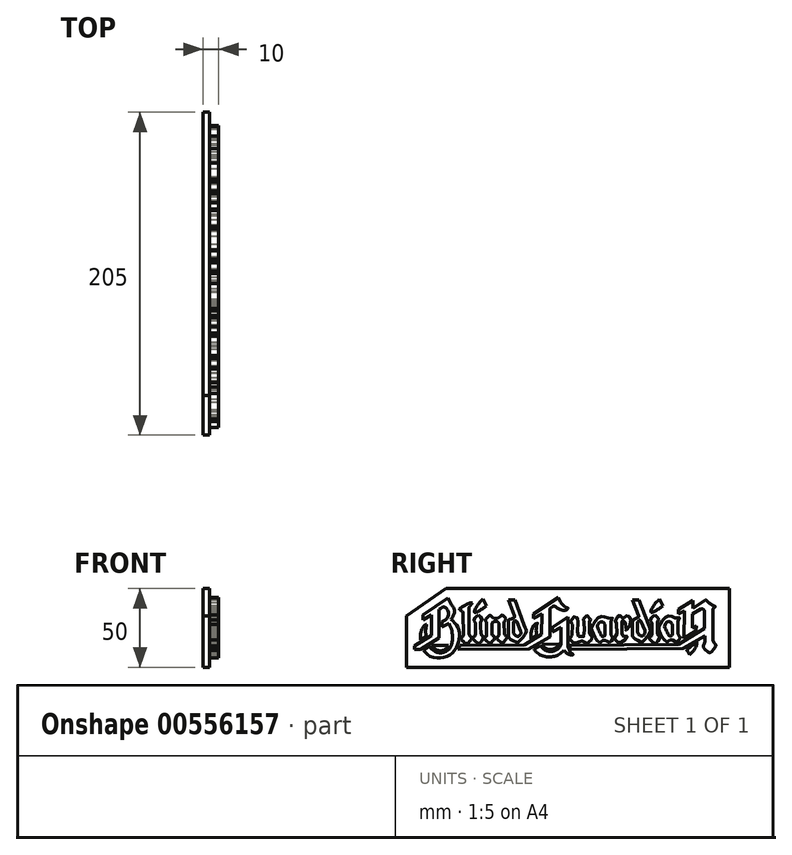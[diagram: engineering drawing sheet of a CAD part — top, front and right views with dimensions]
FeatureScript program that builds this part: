
annotation { "Feature Type Name" : "Feature", "Feature Type Description" : "" }
export const myFeature = defineFeature(function(context is Context, id is Id, definition is map)
    precondition{}
    {
        {
            var Q0;
            Q0=qCreatedBy(makeId("Right.planeOp"),FACE);
            var sketch = newSketch(context, id + "F0", { "sketchPlane" : qUnion([Q0])});
            skLineSegment(sketch, "E0", {"start": v(-84.73, 5.08) * mm, "end": v(-84.73, 8.23) * mm});
            skLineSegment(sketch, "E1", {"start": v(-84.73, 8.23) * mm, "end": v(-68.64, 19.15) * mm});
            skLineSegment(sketch, "E2", {"start": v(-84.73, 5.08) * mm, "end": v(-79.13, 8.3) * mm});
            skLineSegment(sketch, "E3", {"start": v(-79.13, 8.3) * mm, "end": v(-79.13, -4.84) * mm});
            skLineSegment(sketch, "E4", {"start": v(-79.13, -4.84) * mm, "end": v(-90.14, -11.45) * mm});
            skLineSegment(sketch, "E5", {"start": v(-90.14, -11.45) * mm, "end": v(-90.14, -13.8) * mm});
            skLineSegment(sketch, "E6", {"start": v(-90.14, -13.8) * mm, "end": v(-86.17, -13.8) * mm});
            skLineSegment(sketch, "E7", {"start": v(-86.17, -13.8) * mm, "end": v(-74.29, -6.5) * mm});
            skLineSegment(sketch, "E8", {"start": v(-74.29, -6.5) * mm, "end": v(-74.29, 11.65) * mm});
            skFitSpline(sketch, "E9", {"points": [v(-68.64, 19.15) * mm, v(-67.18, 15.64) * mm, v(-65.24, 13) * mm, v(-64.6, 11.06) * mm, v(-65.24, 7.93) * mm, v(-66.75, 5.45) * mm], "startDerivative": vector(5.4, -16.3) * mm, "endDerivative": vector(-8.46, -11.7) * mm});
            skFitSpline(sketch, "E10", {"points": [v(-66.75, 5.45) * mm, v(-64.43, 3.18) * mm, v(-62, -0.73) * mm, v(-61.43, -4.8) * mm, v(-62.17, -9.59) * mm, v(-64.56, -14.4) * mm, v(-69.3, -18.01) * mm, v(-75.07, -19.05) * mm, v(-81.23, -17.36) * mm, v(-84.19, -14.28) * mm], "startDerivative": vector(25.48, -22.56) * mm, "endDerivative": vector(-23.63, 32.62) * mm});
            skLineSegment(sketch, "E11", {"start": v(-84.19, -14.28) * mm, "end": v(-80.47, -11.9) * mm});
            skFitSpline(sketch, "E12", {"points": [v(-80.47, -11.9) * mm, v(-78.16, -14.27) * mm, v(-74.24, -15.81) * mm, v(-69.63, -14.76) * mm, v(-66.48, -10.92) * mm, v(-65.96, -4.87) * mm, v(-66.52, -0.7) * mm, v(-68.23, 3) * mm], "startDerivative": vector(16.74, -20.43) * mm, "endDerivative": vector(-14.61, 26.93) * mm});
            skFitSpline(sketch, "E13", {"points": [v(-74.29, 11.65) * mm, v(-72.46, 13.03) * mm, v(-70.92, 13.2) * mm, v(-68.82, 11.08) * mm, v(-68.76, 7.13) * mm, v(-70.78, 4.75) * mm, v(-72.57, 3.77) * mm], "startDerivative": vector(11.7, 10.28) * mm, "endDerivative": vector(-11.83, -5.55) * mm});
            skLineSegment(sketch, "E14", {"start": v(-68.23, 3) * mm, "end": v(-72.57, 0.76) * mm});
            skLineSegment(sketch, "E15", {"start": v(-72.57, 0.76) * mm, "end": v(-72.57, 3.77) * mm});
            skLineSegment(sketch, "E16", {"start": v(-79.14, -11.26) * mm, "end": v(-68.4, -10.98) * mm});
            skFitSpline(sketch, "E17", {"points": [v(-68.4, -10.98) * mm, v(-69.8, -13.08) * mm, v(-72.6, -14.4) * mm, v(-75.7, -14.13) * mm, v(-77.95, -12.73) * mm, v(-79.14, -11.26) * mm], "startDerivative": vector(-5.81, -11.49) * mm, "endDerivative": vector(-6.19, 8.83) * mm});
            skLineSegment(sketch, "E18", {"start": v(-82.4, -5.4) * mm, "end": v(-86.28, -7.61) * mm});
            skFitSpline(sketch, "E19", {"points": [v(-82.4, -5.4) * mm, v(-82.8, -3.93) * mm, v(-82.85, -1.08) * mm, v(-82.23, 2.17) * mm], "startDerivative": vector(-1.73, 5.13) * mm, "endDerivative": vector(2, 8.42) * mm});
            skFitSpline(sketch, "E20", {"points": [v(-86.28, -7.61) * mm, v(-86.28, -5.4) * mm, v(-85.85, -2.26) * mm, v(-84.59, 0.4) * mm, v(-83.33, 1.73) * mm, v(-82.23, 2.17) * mm], "startDerivative": vector(-0.23, 10.54) * mm, "endDerivative": vector(7.6, 2.22) * mm});
            skFitSpline(sketch, "E21", {"points": [v(-59.1, 9.06) * mm, v(-59.28, 10.1) * mm, v(-60.1, 10.84) * mm, v(-61.1, 11.4) * mm, v(-61.5, 11.83) * mm, v(-60.67, 12.62) * mm, v(-58.24, 14.18) * mm, v(-54.85, 15.7) * mm, v(-53.12, 16) * mm], "startDerivative": vector(-0.2, 10.77) * mm, "endDerivative": vector(11.85, 1.15) * mm});
            skFitSpline(sketch, "E22", {"points": [v(-53.12, 16) * mm, v(-53.9, 14.96) * mm, v(-54.94, 13.57) * mm, v(-55.42, 12.62) * mm, v(-55.46, 11.92) * mm], "startDerivative": vector(-2.78, -3.76) * mm, "endDerivative": vector(0.11, -3.55) * mm});
            skLineSegment(sketch, "E23", {"start": v(-55.46, 11.92) * mm, "end": v(-55.46, -3.28) * mm});
            skLineSegment(sketch, "E24", {"start": v(-59.1, 9.06) * mm, "end": v(-58.91, -4.41) * mm});
            skFitSpline(sketch, "E25", {"points": [v(-58.91, -4.41) * mm, v(-59.17, -5.41) * mm, v(-60.16, -6.23) * mm, v(-60.62, -6.6) * mm, v(-60.41, -7.13) * mm, v(-59.8, -7.86) * mm, v(-58.91, -8.77) * mm, v(-57.4, -10) * mm, v(-56.99, -10.22) * mm, v(-56.42, -9.92) * mm, v(-54.9, -8.63) * mm, v(-53.72, -6.82) * mm, v(-53.59, -6.32) * mm, v(-53.82, -5.96) * mm, v(-54.52, -5.39) * mm, v(-55.08, -4.66) * mm, v(-55.36, -3.82) * mm, v(-55.46, -3.28) * mm], "startDerivative": vector(-1.38, -16.95) * mm, "endDerivative": vector(-1.94, 11.37) * mm});
            skFitSpline(sketch, "E26", {"points": [v(-46.43, 18.3) * mm, v(-47.6, 17.21) * mm, v(-49.28, 15.37) * mm, v(-50.45, 13.61) * mm, v(-51.62, 11.52) * mm, v(-51.95, 10.52) * mm, v(-51.95, 9.89) * mm, v(-51.12, 9.85) * mm, v(-49.6, 10.4) * mm, v(-48.27, 11.19) * mm, v(-46.76, 12.27) * mm, v(-45.43, 13.24) * mm, v(-44.38, 13.95) * mm], "startDerivative": vector(-13.02, -11.66) * mm, "endDerivative": vector(13.48, 9.05) * mm});
            skLineSegment(sketch, "E27", {"start": v(-44.38, 13.95) * mm, "end": v(-46.43, 18.3) * mm});
            skFitSpline(sketch, "E28", {"points": [v(-49.36, 8.34) * mm, v(-50.32, 7.67) * mm, v(-51.53, 6.42) * mm, v(-52.46, 5.08) * mm, v(-51.53, 3.74) * mm, v(-51.37, 2.73) * mm, v(-51.28, -3.96) * mm, v(-51.45, -4.63) * mm, v(-52.04, -5.47) * mm, v(-53.2, -6.22) * mm, v(-52.88, -6.96) * mm, v(-51.47, -8.5) * mm, v(-50.33, -9.43) * mm, v(-49.4, -10.02) * mm, v(-48.65, -9.53) * mm, v(-47.13, -8.04) * mm, v(-46.26, -6.5) * mm, v(-46.1, -5.95) * mm, v(-47.08, -5.03) * mm, v(-47.67, -4.38) * mm, v(-47.84, -3.24) * mm, v(-47.94, 3.03) * mm, v(-47.78, 3.92) * mm, v(-47.21, 4.84) * mm, v(-46.97, 5.17) * mm, v(-47.02, 5.55) * mm, v(-48.13, 6.93) * mm, v(-49.36, 8.34) * mm]});
            skLineSegment(sketch, "E29", {"start": v(-44.12, 3.65) * mm, "end": v(-44.12, -4.8) * mm});
            skLineSegment(sketch, "E30", {"start": v(-40.75, 2.67) * mm, "end": v(-40.75, -3.66) * mm});
            skLineSegment(sketch, "E31", {"start": v(-36.33, 2.6) * mm, "end": v(-36.33, -4.34) * mm});
            skLineSegment(sketch, "E32", {"start": v(-33.03, 3.34) * mm, "end": v(-32.9, -3.77) * mm});
            skFitSpline(sketch, "E33", {"points": [v(-33.03, 3.34) * mm, v(-32.77, 4.26) * mm, v(-32.17, 5.1) * mm, v(-32, 5.39) * mm, v(-32.07, 5.74) * mm, v(-33.17, 7.2) * mm, v(-34.04, 8.1) * mm, v(-34.3, 8.27) * mm, v(-34.65, 8.12) * mm, v(-35.37, 7.4) * mm, v(-36.57, 6.48) * mm, v(-37.62, 6.02) * mm, v(-38.75, 5.99) * mm, v(-40.12, 6.44) * mm, v(-41.35, 7.36) * mm, v(-41.86, 7.92) * mm, v(-42, 8.06) * mm, v(-42.15, 8.12) * mm, v(-42.4, 8) * mm, v(-43.13, 7.34) * mm, v(-43.9, 6.48) * mm, v(-44.6, 5.6) * mm, v(-44.9, 5.21) * mm, v(-44.96, 5.04) * mm, v(-44.82, 4.72) * mm, v(-44.52, 4.25) * mm, v(-44.33, 3.98) * mm, v(-44.12, 3.65) * mm], "startDerivative": vector(3.75, 21.25) * mm, "endDerivative": vector(7.67, -12.75) * mm});
            skFitSpline(sketch, "E34", {"points": [v(-40.75, 2.67) * mm, v(-40.28, 3.54) * mm, v(-39.14, 4.03) * mm, v(-37.8, 4.07) * mm, v(-36.76, 3.49) * mm, v(-36.33, 2.6) * mm], "startDerivative": vector(1.78, 5.2) * mm, "endDerivative": vector(1.63, -5.1) * mm});
            skFitSpline(sketch, "E35", {"points": [v(-32.9, -3.77) * mm, v(-32.57, -4.4) * mm, v(-32, -5.08) * mm, v(-31.39, -5.6) * mm, v(-31.16, -5.82) * mm, v(-31.27, -6.2) * mm, v(-31.88, -7.3) * mm, v(-33.27, -8.8) * mm, v(-34.08, -9.4) * mm, v(-34.47, -9.62) * mm, v(-34.78, -9.44) * mm, v(-35.63, -8.77) * mm, v(-36.93, -7.64) * mm, v(-37.81, -6.55) * mm, v(-37.95, -6.27) * mm, v(-37.72, -5.97) * mm, v(-36.93, -5.43) * mm, v(-36.33, -4.87) * mm, v(-36.33, -4.55) * mm, v(-36.33, -4.34) * mm], "startDerivative": vector(5.52, -12.4) * mm, "endDerivative": vector(0.48, 7.16) * mm});
            skFitSpline(sketch, "E36", {"points": [v(-40.75, -3.66) * mm, v(-40.59, -4.34) * mm, v(-39.9, -5.08) * mm, v(-39.1, -5.69) * mm, v(-38.84, -5.89) * mm, v(-38.93, -6.28) * mm, v(-39.52, -7.37) * mm, v(-41.46, -9.3) * mm, v(-42.08, -9.73) * mm, v(-42.34, -9.73) * mm, v(-42.84, -9.47) * mm, v(-45.13, -7.41) * mm, v(-45.61, -6.72) * mm, v(-45.64, -6.39) * mm, v(-45.27, -6.02) * mm, v(-44.5, -5.4) * mm, v(-44.12, -5.08) * mm, v(-44.12, -4.8) * mm], "startDerivative": vector(1.18, -12.53) * mm, "endDerivative": vector(-1.63, 8.17) * mm});
            skFitSpline(sketch, "E37", {"points": [v(-26.5, 7.68) * mm, v(-26.37, 7.09) * mm, v(-26.48, 6.65) * mm, v(-27.5, 6.19) * mm, v(-28.84, 5.6) * mm, v(-29.9, 5) * mm, v(-30.38, 4.34) * mm, v(-30.44, 3.34) * mm, v(-30.43, -5.08) * mm, v(-30.4, -5.49) * mm, v(-29.76, -6.52) * mm, v(-27.07, -8.3) * mm, v(-25.06, -9.14) * mm, v(-24.72, -9.24) * mm, v(-24.38, -9.18) * mm, v(-23.02, -7.9) * mm, v(-20.64, -5.23) * mm, v(-19.05, -2.95) * mm, v(-18.92, -2.3) * mm, v(-19.1, -1.2) * mm, v(-19.5, -0.04) * mm, v(-20.36, 1.92) * mm], "startDerivative": vector(5.75, -19.57) * mm, "endDerivative": vector(-15.94, 36.18) * mm});
            skLineSegment(sketch, "E38", {"start": v(-26.5, 7.68) * mm, "end": v(-30.31, 17.65) * mm});
            skLineSegment(sketch, "E39", {"start": v(-30.31, 17.65) * mm, "end": v(-26.19, 17.65) * mm});
            skLineSegment(sketch, "E40", {"start": v(-26.19, 17.65) * mm, "end": v(-20.36, 1.92) * mm});
            skLineSegment(sketch, "E41", {"start": v(-27.18, -2.48) * mm, "end": v(-27.18, 3.19) * mm});
            skLineSegment(sketch, "E42", {"start": v(-25, 3.9) * mm, "end": v(-22.62, -1.86) * mm});
            skFitSpline(sketch, "E43", {"points": [v(-27.18, 3.19) * mm, v(-26.96, 3.92) * mm, v(-26.3, 4.44) * mm, v(-25.44, 4.46) * mm, v(-25, 3.9) * mm], "startDerivative": vector(0.53, 3.15) * mm, "endDerivative": vector(1.42, -2.93) * mm});
            skFitSpline(sketch, "E44", {"points": [v(-22.62, -1.86) * mm, v(-22.43, -2.56) * mm, v(-22.43, -3.43) * mm, v(-23.62, -5.17) * mm, v(-24, -5.39) * mm, v(-24.6, -5.39) * mm, v(-25.58, -4.98) * mm, v(-26.44, -4.36) * mm, v(-27.1, -3.27) * mm, v(-27.18, -2.48) * mm], "startDerivative": vector(1.99, -7.25) * mm, "endDerivative": vector(0.09, 7.38) * mm});
            skFitSpline(sketch, "E45", {"points": [v(-12.08, -4.65) * mm, v(-12.67, -2.48) * mm, v(-12.58, -0.04) * mm, v(-11.91, 3.05) * mm, v(-11.86, 3.14) * mm, v(-12.2, 3.02) * mm, v(-13.75, 1.95) * mm, v(-15.06, -0.04) * mm, v(-15.73, -2.07) * mm, v(-15.95, -4.23) * mm, v(-16, -6.42) * mm, v(-16.01, -6.71) * mm, v(-16.01, -6.8) * mm, v(-13.95, -5.58) * mm, v(-12.27, -4.7) * mm], "startDerivative": vector(-8.11, 24.7) * mm, "endDerivative": vector(17.5, 8) * mm});
            skLineSegment(sketch, "E46", {"start": v(-12.27, -4.7) * mm, "end": v(-12.08, -4.65) * mm});
            skLineSegment(sketch, "E47", {"start": v(-8.92, -10.51) * mm, "end": v(1.73, -10.24) * mm});
            skArc(sketch, "E48", {"start": v(-8.92, -10.51) * mm, "mid": v(-3.5, -13.74) * mm, "end": v(1.73, -10.24) * mm});
            skLineSegment(sketch, "E49", {"start": v(-62.44, -13.6) * mm, "end": v(-61.23, -11.18) * mm});
            skLineSegment(sketch, "E50", {"start": v(-61.23, -11.18) * mm, "end": v(-20.11, -10.87) * mm});
            skLineSegment(sketch, "E51", {"start": v(-20.11, -10.87) * mm, "end": v(-9.26, -4.14) * mm});
            skLineSegment(sketch, "E52", {"start": v(-9.26, -4.14) * mm, "end": v(-8.92, 8.96) * mm});
            skLineSegment(sketch, "E53", {"start": v(-8.92, 8.96) * mm, "end": v(-14.41, 6) * mm});
            skLineSegment(sketch, "E54", {"start": v(-14.41, 6) * mm, "end": v(-14.49, 8.88) * mm});
            skLineSegment(sketch, "E55", {"start": v(-14.49, 8.88) * mm, "end": v(1.35, 19.49) * mm});
            skLineSegment(sketch, "E56", {"start": v(-3.84, 12.28) * mm, "end": v(-3.84, -5.2) * mm});
            skLineSegment(sketch, "E57", {"start": v(-62.44, -13.6) * mm, "end": v(-17.17, -13.28) * mm});
            skLineSegment(sketch, "E58", {"start": v(-17.17, -13.28) * mm, "end": v(-4.43, -6.18) * mm});
            skFitSpline(sketch, "E59", {"points": [v(-4.43, -6.18) * mm, v(-4, -5.78) * mm, v(-3.84, -5.2) * mm], "startDerivative": vector(1, 0.73) * mm, "endDerivative": vector(0.2, 1.22) * mm});
            skFitSpline(sketch, "E60", {"points": [v(-3.84, 12.28) * mm, v(-2.14, 13.6) * mm, v(-1.54, 13.8) * mm, v(-0.94, 13.78) * mm, v(-0.17, 13.29) * mm, v(0.9, 12.48) * mm, v(2.68, 11.54) * mm, v(4.55, 11.25) * mm, v(6.3, 11.46) * mm, v(7.47, 12.28) * mm, v(7.62, 12.5) * mm, v(7.64, 12.55) * mm, v(6.1, 13.15) * mm, v(4.2, 14.6) * mm, v(2.78, 16.44) * mm, v(1.55, 18.96) * mm, v(1.35, 19.49) * mm], "startDerivative": vector(23.38, 19.98) * mm, "endDerivative": vector(-3.54, 9.98) * mm});
            skFitSpline(sketch, "E61", {"points": [v(52.4, 7.87) * mm, v(52.54, 7.28) * mm, v(52.43, 6.85) * mm, v(51.4, 6.38) * mm, v(50.07, 5.79) * mm, v(49, 5.2) * mm, v(48.52, 4.54) * mm, v(48.47, 3.54) * mm, v(48.47, -4.88) * mm, v(48.5, -5.3) * mm, v(49.14, -6.32) * mm, v(51.83, -8.1) * mm, v(53.85, -8.95) * mm, v(54.19, -9.04) * mm, v(54.53, -8.99) * mm, v(55.89, -7.71) * mm, v(58.27, -5.04) * mm, v(59.85, -2.76) * mm, v(59.98, -2.1) * mm, v(59.81, -1.01) * mm, v(59.4, 0.16) * mm, v(58.55, 2.12) * mm], "startDerivative": vector(5.75, -19.57) * mm, "endDerivative": vector(-15.94, 36.18) * mm});
            skLineSegment(sketch, "E62", {"start": v(52.4, 7.87) * mm, "end": v(48.6, 17.85) * mm});
            skLineSegment(sketch, "E63", {"start": v(48.6, 17.85) * mm, "end": v(52.72, 17.85) * mm});
            skLineSegment(sketch, "E64", {"start": v(52.72, 17.85) * mm, "end": v(58.55, 2.12) * mm});
            skLineSegment(sketch, "E65", {"start": v(51.73, -2.29) * mm, "end": v(51.73, 3.38) * mm});
            skLineSegment(sketch, "E66", {"start": v(53.9, 4.09) * mm, "end": v(56.29, -1.67) * mm});
            skFitSpline(sketch, "E67", {"points": [v(51.73, 3.38) * mm, v(51.95, 4.11) * mm, v(52.6, 4.63) * mm, v(53.46, 4.66) * mm, v(53.9, 4.09) * mm], "startDerivative": vector(0.53, 3.15) * mm, "endDerivative": vector(1.42, -2.93) * mm});
            skFitSpline(sketch, "E68", {"points": [v(56.29, -1.67) * mm, v(56.48, -2.37) * mm, v(56.48, -3.24) * mm, v(55.28, -4.98) * mm, v(54.9, -5.2) * mm, v(54.3, -5.2) * mm, v(53.33, -4.79) * mm, v(52.46, -4.16) * mm, v(51.8, -3.08) * mm, v(51.73, -2.29) * mm], "startDerivative": vector(1.99, -7.25) * mm, "endDerivative": vector(0.09, 7.38) * mm});
            skFitSpline(sketch, "E69", {"points": [v(65.7, 18.33) * mm, v(64.53, 17.24) * mm, v(62.86, 15.4) * mm, v(61.69, 13.65) * mm, v(60.52, 11.55) * mm, v(60.18, 10.55) * mm, v(60.18, 9.92) * mm, v(61.02, 9.88) * mm, v(62.53, 10.42) * mm, v(63.86, 11.22) * mm, v(65.37, 12.3) * mm, v(66.7, 13.27) * mm, v(67.76, 13.98) * mm], "startDerivative": vector(-13.02, -11.66) * mm, "endDerivative": vector(13.48, 9.05) * mm});
            skLineSegment(sketch, "E70", {"start": v(67.76, 13.98) * mm, "end": v(65.7, 18.33) * mm});
            skFitSpline(sketch, "E71", {"points": [v(62.78, 8.37) * mm, v(61.81, 7.7) * mm, v(60.6, 6.45) * mm, v(59.68, 5.1) * mm, v(60.6, 3.77) * mm, v(60.77, 2.77) * mm, v(60.85, -3.93) * mm, v(60.68, -4.6) * mm, v(60.1, -5.43) * mm, v(58.93, -6.19) * mm, v(59.25, -6.92) * mm, v(60.66, -8.47) * mm, v(61.8, -9.4) * mm, v(62.73, -9.99) * mm, v(63.49, -9.5) * mm, v(65, -8) * mm, v(65.87, -6.46) * mm, v(66.04, -5.92) * mm, v(65.06, -5) * mm, v(64.46, -4.35) * mm, v(64.3, -3.2) * mm, v(64.2, 3.06) * mm, v(64.35, 3.96) * mm, v(64.92, 4.88) * mm, v(65.17, 5.2) * mm, v(65.11, 5.58) * mm, v(64, 6.97) * mm, v(62.78, 8.37) * mm]});
            skLineSegment(sketch, "E72", {"start": v(2.94, -10.45) * mm, "end": v(3.12, 0.38) * mm});
            skLineSegment(sketch, "E73", {"start": v(3.12, 0.38) * mm, "end": v(-2.25, -2.44) * mm});
            skLineSegment(sketch, "E74", {"start": v(-2.25, -2.44) * mm, "end": v(-2.25, 0.38) * mm});
            skLineSegment(sketch, "E75", {"start": v(-2.25, 0.38) * mm, "end": v(7.42, 6.85) * mm});
            skLineSegment(sketch, "E76", {"start": v(7.42, 6.85) * mm, "end": v(7.42, -10.2) * mm});
            skFitSpline(sketch, "E77", {"points": [v(7.42, -10.2) * mm, v(7.63, -12.34) * mm, v(9.05, -15.25) * mm, v(10.63, -17.04) * mm, v(10.72, -17.11) * mm, v(10.6, -17.11) * mm, v(9.17, -17.04) * mm, v(6.72, -16.08) * mm, v(5.06, -14.44) * mm], "startDerivative": vector(0.17, -13.92) * mm, "endDerivative": vector(-9.57, 11.37) * mm});
            skLineSegment(sketch, "E78", {"start": v(-14.13, -13.4) * mm, "end": v(-10.36, -11.11) * mm});
            skFitSpline(sketch, "E79", {"points": [v(-14.13, -13.4) * mm, v(-12.99, -15.09) * mm, v(-10.5, -16.89) * mm, v(-7.4, -18.12) * mm, v(-4, -18.42) * mm, v(-0.9, -17.92) * mm, v(2.07, -16.64) * mm, v(4.47, -14.82) * mm, v(5.06, -14.44) * mm], "startDerivative": vector(8.5, -15.86) * mm, "endDerivative": vector(7.8, 4.28) * mm});
            skFitSpline(sketch, "E80", {"points": [v(-10.36, -11.11) * mm, v(-8.28, -13.14) * mm, v(-5.18, -14.72) * mm, v(-1.61, -14.68) * mm, v(1.51, -12.97) * mm, v(2.94, -10.45) * mm], "startDerivative": vector(10.06, -11.04) * mm, "endDerivative": vector(6.18, 13.54) * mm});
            skFitSpline(sketch, "E81", {"points": [v(10.19, -4.82) * mm, v(10.25, 1.64) * mm, v(10.25, 2.47) * mm, v(10.16, 2.86) * mm, v(9.72, 3.7) * mm, v(9.29, 4.17) * mm, v(9.11, 4.46) * mm, v(9.37, 4.83) * mm, v(10.8, 6.72) * mm, v(11.81, 7.6) * mm, v(12.15, 7.76) * mm, v(12.55, 7.5) * mm, v(14.24, 5.47) * mm, v(14.57, 4.96) * mm, v(14.1, 4.12) * mm, v(13.7, 3.14) * mm, v(13.56, -0.76) * mm, v(13.63, -4) * mm, v(13.67, -4.54) * mm, v(14.07, -5.21) * mm, v(15.28, -5.99) * mm, v(16.4, -6.02) * mm, v(17.47, -5.48) * mm, v(17.94, -4.74) * mm, v(17.98, -3.16) * mm, v(17.94, 2.13) * mm, v(17.94, 2.8) * mm, v(17.6, 3.62) * mm, v(16.87, 4.5) * mm, v(16.78, 4.76) * mm, v(17.25, 5.48) * mm, v(18.18, 6.59) * mm, v(19.32, 7.65) * mm, v(19.6, 7.82) * mm, v(19.9, 7.78) * mm, v(20.79, 6.86) * mm, v(21.58, 5.85) * mm, v(21.98, 5.28) * mm, v(22.1, 5.09) * mm, v(22, 4.83) * mm, v(21.43, 4.04) * mm, v(21.3, 3.84) * mm, v(21.24, 3.46) * mm, v(21.28, -3.67) * mm, v(21.28, -3.92) * mm, v(21.63, -4.78) * mm, v(22.58, -5.52) * mm, v(23.15, -5.63) * mm, v(23.26, -5.63) * mm, v(23.28, -5.82) * mm, v(22.97, -6.84) * mm, v(21.6, -8.54) * mm, v(20.08, -9.75) * mm, v(19.84, -9.83) * mm, v(19.5, -9.66) * mm, v(18.45, -8.95) * mm, v(16.83, -8.25) * mm, v(15.87, -8.08) * mm, v(14.57, -8.27) * mm, v(12.33, -9.73) * mm, v(11.97, -10.13) * mm, v(11.77, -10.2) * mm, v(11.12, -9.78) * mm, v(9.8, -8.64) * mm, v(8.74, -7.43) * mm, v(8.52, -7.13) * mm, v(8.57, -6.77) * mm, v(9.42, -6.22) * mm, v(10.12, -5.53) * mm, v(10.19, -4.82) * mm]});
            skFitSpline(sketch, "E82", {"points": [v(36.88, -6.22) * mm, v(38.1, -5.21) * mm, v(38.45, -4.03) * mm, v(38.4, 2.82) * mm, v(38.38, 3.27) * mm, v(38.27, 3.67) * mm, v(37.56, 4.55) * mm, v(37.39, 4.75) * mm, v(37.4, 5.05) * mm, v(39.2, 7.26) * mm, v(39.98, 7.94) * mm, v(40.22, 8.05) * mm, v(40.57, 7.9) * mm, v(41.8, 6.65) * mm, v(42.32, 6.06) * mm, v(42.5, 5.97) * mm, v(42.67, 6.1) * mm, v(44.02, 7.28) * mm, v(44.96, 7.96) * mm, v(45.29, 8.07) * mm, v(45.64, 7.8) * mm, v(46.51, 6.85) * mm, v(47.3, 5.75) * mm, v(47.56, 4.46) * mm, v(47.21, 2.72) * mm, v(46.51, 1.08) * mm, v(45.55, -0.32) * mm, v(44.41, -1.41) * mm, v(44.27, -1.54) * mm, v(44.27, -1.41) * mm, v(44.32, 0.79) * mm, v(44.23, 2.3) * mm, v(43.38, 4.04) * mm, v(42.81, 4.72) * mm, v(42.55, 4.8) * mm, v(42.16, 4.55) * mm, v(41.8, 3.98) * mm, v(41.72, 2.71) * mm, v(41.73, -3.84) * mm, v(41.77, -4.09) * mm, v(42.2, -4.8) * mm, v(42.99, -5.39) * mm, v(44, -5.43) * mm, v(44.94, -5.43) * mm, v(45.11, -5.45) * mm, v(45.09, -5.57) * mm, v(44.65, -6.52) * mm, v(43.71, -7.57) * mm, v(42.48, -8.48) * mm, v(41.06, -9.3) * mm, v(40.23, -9.65) * mm, v(40.07, -9.67) * mm, v(39.76, -9.56) * mm, v(38.68, -8.77) * mm, v(37.98, -8.1) * mm, v(37.13, -7.2) * mm, v(36.67, -6.67) * mm, v(36.64, -6.52) * mm, v(36.7, -6.35) * mm, v(36.88, -6.22) * mm]});
            skFitSpline(sketch, "E83", {"points": [v(9.29, -13.57) * mm, v(8.85, -12.68) * mm, v(8.6, -11.78) * mm, v(8.6, -11.08) * mm], "startDerivative": vector(-1.32, 2.47) * mm, "endDerivative": vector(0.14, 2.27) * mm});
            skFitSpline(sketch, "E84", {"points": [v(36.17, -6.62) * mm, v(35.43, -7.8) * mm, v(34.32, -8.79) * mm, v(33.67, -9.2) * mm, v(33.26, -9.06) * mm, v(32.37, -8.51) * mm, v(31.28, -7.92) * mm, v(30.52, -7.78) * mm, v(29.57, -7.97) * mm, v(28.68, -8.57) * mm, v(28.13, -8.98) * mm, v(27.86, -9.22) * mm, v(27.27, -8.87) * mm, v(25.96, -7.8) * mm, v(24.66, -5.96) * mm, v(23.69, -4.12) * mm, v(22.65, -1.68) * mm, v(22.38, -0.32) * mm, v(23.17, 1.69) * mm, v(24.34, 3.78) * mm, v(26, 5.81) * mm, v(27.94, 7.11) * mm, v(29.7, 7.33) * mm, v(31.6, 6.7) * mm, v(33.29, 6.06) * mm, v(34.65, 6.03) * mm, v(35.65, 6.06) * mm, v(35.8, 6.07) * mm, v(35.75, 5.92) * mm, v(35.18, 5.26) * mm, v(34.8, 4.71) * mm, v(34.67, 3.9) * mm, v(34.67, 0.82) * mm], "startDerivative": vector(-19.03, -37.74) * mm, "endDerivative": vector(0.67, -72.98) * mm});
            skFitSpline(sketch, "E85", {"points": [v(34.67, 0.82) * mm, v(34.67, -3.03) * mm, v(34.67, -3.66) * mm, v(34.67, -4.07) * mm, v(35.32, -5.2) * mm, v(35.94, -5.91) * mm, v(36.21, -6.26) * mm, v(36.17, -6.62) * mm], "startDerivative": vector(-0.08, -16.07) * mm, "endDerivative": vector(-1.27, -4.14) * mm});
            skFitSpline(sketch, "E86", {"points": [v(31, -4.46) * mm, v(30.74, -5.13) * mm, v(29.95, -5.46) * mm, v(28.95, -5.13) * mm, v(28.07, -3.62) * mm, v(27.15, -1.7) * mm, v(26.27, 0.4) * mm, v(26.23, 1.4) * mm, v(27.06, 2.9) * mm, v(28.23, 3.74) * mm, v(29.4, 3.74) * mm, v(30.41, 2.99) * mm, v(31.08, 1.82) * mm, v(31.08, 1.27) * mm, v(31, -4.46) * mm]});
            skFitSpline(sketch, "E87", {"points": [v(78.86, -6.38) * mm, v(78.13, -7.57) * mm, v(77.02, -8.55) * mm, v(76.36, -8.96) * mm, v(75.96, -8.82) * mm, v(75.06, -8.28) * mm, v(73.98, -7.68) * mm, v(73.22, -7.55) * mm, v(72.27, -7.74) * mm, v(71.37, -8.33) * mm, v(70.83, -8.74) * mm, v(70.56, -8.99) * mm, v(69.96, -8.63) * mm, v(68.66, -7.57) * mm, v(67.36, -5.73) * mm, v(66.38, -3.89) * mm, v(65.35, -1.44) * mm, v(65.08, -0.09) * mm, v(65.86, 1.92) * mm, v(67.03, 4.01) * mm, v(68.69, 6.04) * mm, v(70.64, 7.35) * mm, v(72.4, 7.56) * mm, v(74.3, 6.94) * mm, v(75.98, 6.29) * mm, v(77.34, 6.26) * mm, v(78.34, 6.3) * mm, v(78.5, 6.3) * mm, v(78.44, 6.15) * mm, v(77.88, 5.5) * mm, v(77.5, 4.95) * mm, v(77.37, 4.14) * mm, v(77.36, 1.05) * mm], "startDerivative": vector(-19.03, -37.74) * mm, "endDerivative": vector(0.67, -72.98) * mm});
            skFitSpline(sketch, "E88", {"points": [v(77.36, 1.05) * mm, v(77.36, -2.8) * mm, v(77.36, -3.42) * mm, v(77.36, -3.83) * mm, v(78.01, -4.97) * mm, v(78.64, -5.68) * mm, v(78.9, -6.03) * mm, v(78.86, -6.38) * mm], "startDerivative": vector(-0.08, -16.07) * mm, "endDerivative": vector(-1.27, -4.14) * mm});
            skFitSpline(sketch, "E89", {"points": [v(73.7, -4.22) * mm, v(73.44, -4.9) * mm, v(72.64, -5.23) * mm, v(71.64, -4.9) * mm, v(70.76, -3.39) * mm, v(69.84, -1.46) * mm, v(68.96, 0.63) * mm, v(68.92, 1.63) * mm, v(69.76, 3.14) * mm, v(70.93, 3.98) * mm, v(72.1, 3.98) * mm, v(73.1, 3.22) * mm, v(73.77, 2.05) * mm, v(73.77, 1.5) * mm, v(73.7, -4.22) * mm]});
            skFitSpline(sketch, "E90", {"points": [v(84.7, -17.25) * mm, v(85.85, -16.04) * mm, v(87.6, -14.05) * mm, v(88.95, -11.59) * mm, v(89.66, -9.64) * mm, v(89.7, -9.31) * mm, v(89, -9.6) * mm, v(86.8, -10.97) * mm, v(84.35, -12.73) * mm, v(82.89, -13.85) * mm, v(82.73, -14) * mm, v(83.55, -15.04) * mm, v(84.42, -16.28) * mm, v(84.61, -16.85) * mm, v(84.68, -17.16) * mm], "startDerivative": vector(13.55, 14.48) * mm, "endDerivative": vector(1.8, -8.49) * mm});
            skLineSegment(sketch, "E91", {"start": v(84.7, -17.25) * mm, "end": v(84.68, -17.16) * mm});
            skLineSegment(sketch, "E92", {"start": v(94.47, -8.66) * mm, "end": v(94.47, -5.23) * mm});
            skLineSegment(sketch, "E93", {"start": v(94.47, -5.23) * mm, "end": v(80.54, -13.08) * mm});
            skLineSegment(sketch, "E94", {"start": v(80.54, -13.08) * mm, "end": v(9.29, -13.57) * mm});
            skLineSegment(sketch, "E95", {"start": v(8.6, -11.08) * mm, "end": v(77.7, -10.63) * mm});
            skLineSegment(sketch, "E96", {"start": v(77.7, -10.63) * mm, "end": v(94.17, -0.28) * mm});
            skLineSegment(sketch, "E97", {"start": v(94.17, -0.28) * mm, "end": v(94.31, 10.77) * mm});
            skLineSegment(sketch, "E98", {"start": v(94.9, 17.88) * mm, "end": v(86.87, 12.32) * mm});
            skLineSegment(sketch, "E99", {"start": v(86.87, 12.32) * mm, "end": v(86.87, 17.55) * mm});
            skLineSegment(sketch, "E100", {"start": v(86.87, 17.55) * mm, "end": v(77.62, 11.82) * mm});
            skLineSegment(sketch, "E101", {"start": v(77.62, 11.82) * mm, "end": v(77.62, 8.8) * mm});
            skLineSegment(sketch, "E102", {"start": v(77.62, 8.8) * mm, "end": v(81.5, 10.8) * mm});
            skLineSegment(sketch, "E103", {"start": v(81.5, 10.8) * mm, "end": v(81.15, -6.8) * mm});
            skLineSegment(sketch, "E104", {"start": v(81.15, -6.8) * mm, "end": v(88.92, -1.88) * mm});
            skLineSegment(sketch, "E105", {"start": v(88.92, -1.88) * mm, "end": v(88.98, 1.25) * mm});
            skPoint(sketch, "E106.visualSharp", {"position": v(86.72, 6.61) * mm});
            skLineSegment(sketch, "E107", {"start": v(88.98, 1.25) * mm, "end": v(86.6, -0.04) * mm});
            skLineSegment(sketch, "E108", {"start": v(86.6, -0.04) * mm, "end": v(86.6, 9.03) * mm});
            skLineSegment(sketch, "E109", {"start": v(86.6, 9.03) * mm, "end": v(91.92, 12.18) * mm});
            skFitSpline(sketch, "E110", {"points": [v(94.31, 10.77) * mm, v(93.78, 11.46) * mm, v(92.9, 12.07) * mm, v(91.92, 12.18) * mm], "startDerivative": vector(-1.51, 2.2) * mm, "endDerivative": vector(-2.98, -0.02) * mm});
            skFitSpline(sketch, "E111", {"points": [v(94.9, 17.88) * mm, v(95.86, 16.94) * mm, v(97.67, 15.48) * mm, v(100.03, 14.04) * mm, v(100.92, 13.64) * mm, v(101.03, 13.6) * mm, v(100.97, 13.53) * mm, v(100.3, 12.85) * mm, v(99.65, 12.18) * mm, v(99.6, 12.09) * mm, v(99.59, 11.92) * mm, v(99.45, -7.01) * mm, v(99.45, -7.52) * mm, v(99.45, -7.93) * mm, v(99.87, -8.9) * mm, v(101.12, -10.45) * mm, v(101.63, -10.86) * mm, v(101.54, -11.23) * mm, v(99.49, -14.18) * mm, v(98.17, -15.58) * mm, v(97.83, -15.82) * mm, v(97.35, -15.68) * mm, v(94.9, -13.92) * mm, v(93.58, -12.45) * mm, v(93.36, -11.43) * mm, v(93.58, -10.47) * mm, v(94.31, -9.59) * mm, v(94.47, -8.66) * mm], "startDerivative": vector(22.84, -23.48) * mm, "endDerivative": vector(0.1, 30.15) * mm});
            skFitSpline(sketch, "E112", {"points": [v(-68.64, 19.15) * mm, v(-67.18, 15.64) * mm, v(-65.24, 13) * mm, v(-64.6, 11.06) * mm, v(-65.24, 7.93) * mm, v(-66.75, 5.45) * mm], "startDerivative": vector(5.4, -16.3) * mm, "endDerivative": vector(-8.46, -11.7) * mm});
            skFitSpline(sketch, "E113", {"points": [v(-66.75, 5.45) * mm, v(-64.43, 3.18) * mm, v(-62, -0.73) * mm, v(-61.43, -4.8) * mm, v(-62.17, -9.59) * mm, v(-64.56, -14.4) * mm, v(-69.3, -18.01) * mm, v(-75.07, -19.05) * mm, v(-81.23, -17.36) * mm, v(-84.19, -14.28) * mm], "startDerivative": vector(25.48, -22.56) * mm, "endDerivative": vector(-23.63, 32.62) * mm});
            skFitSpline(sketch, "E114", {"points": [v(-80.47, -11.9) * mm, v(-78.16, -14.27) * mm, v(-74.24, -15.81) * mm, v(-69.63, -14.76) * mm, v(-66.48, -10.92) * mm, v(-65.96, -4.87) * mm, v(-66.52, -0.7) * mm, v(-68.23, 3) * mm], "startDerivative": vector(16.74, -20.43) * mm, "endDerivative": vector(-14.61, 26.93) * mm});
            skFitSpline(sketch, "E115", {"points": [v(-74.29, 11.65) * mm, v(-72.46, 13.03) * mm, v(-70.92, 13.2) * mm, v(-68.82, 11.08) * mm, v(-68.76, 7.13) * mm, v(-70.78, 4.75) * mm, v(-72.57, 3.77) * mm], "startDerivative": vector(11.7, 10.28) * mm, "endDerivative": vector(-11.83, -5.55) * mm});
            skFitSpline(sketch, "E116", {"points": [v(-68.4, -10.98) * mm, v(-69.8, -13.08) * mm, v(-72.6, -14.4) * mm, v(-75.7, -14.13) * mm, v(-77.95, -12.73) * mm, v(-79.14, -11.26) * mm], "startDerivative": vector(-5.81, -11.49) * mm, "endDerivative": vector(-6.19, 8.83) * mm});
            skFitSpline(sketch, "E117", {"points": [v(-82.4, -5.4) * mm, v(-82.8, -3.93) * mm, v(-82.85, -1.08) * mm, v(-82.23, 2.17) * mm], "startDerivative": vector(-1.73, 5.13) * mm, "endDerivative": vector(2, 8.42) * mm});
            skFitSpline(sketch, "E118", {"points": [v(-86.28, -7.61) * mm, v(-86.28, -5.4) * mm, v(-85.85, -2.26) * mm, v(-84.59, 0.4) * mm, v(-83.33, 1.73) * mm, v(-82.23, 2.17) * mm], "startDerivative": vector(-0.23, 10.54) * mm, "endDerivative": vector(7.6, 2.22) * mm});
            skFitSpline(sketch, "E119", {"points": [v(-59.1, 9.06) * mm, v(-59.28, 10.1) * mm, v(-60.1, 10.84) * mm, v(-61.1, 11.4) * mm, v(-61.5, 11.83) * mm, v(-60.67, 12.62) * mm, v(-58.24, 14.18) * mm, v(-54.85, 15.7) * mm, v(-53.12, 16) * mm], "startDerivative": vector(-0.2, 10.77) * mm, "endDerivative": vector(11.85, 1.15) * mm});
            skFitSpline(sketch, "E120", {"points": [v(-53.12, 16) * mm, v(-53.9, 14.96) * mm, v(-54.94, 13.57) * mm, v(-55.42, 12.62) * mm, v(-55.46, 11.92) * mm], "startDerivative": vector(-2.78, -3.76) * mm, "endDerivative": vector(0.11, -3.55) * mm});
            skFitSpline(sketch, "E121", {"points": [v(-58.91, -4.41) * mm, v(-59.17, -5.41) * mm, v(-60.16, -6.23) * mm, v(-60.62, -6.6) * mm, v(-60.41, -7.13) * mm, v(-59.8, -7.86) * mm, v(-58.91, -8.77) * mm, v(-57.4, -10) * mm, v(-56.99, -10.22) * mm, v(-56.42, -9.92) * mm, v(-54.9, -8.63) * mm, v(-53.72, -6.82) * mm, v(-53.59, -6.32) * mm, v(-53.82, -5.96) * mm, v(-54.52, -5.39) * mm, v(-55.08, -4.66) * mm, v(-55.36, -3.82) * mm, v(-55.46, -3.28) * mm], "startDerivative": vector(-1.38, -16.95) * mm, "endDerivative": vector(-1.94, 11.37) * mm});
            skFitSpline(sketch, "E122", {"points": [v(-46.43, 18.3) * mm, v(-47.6, 17.21) * mm, v(-49.28, 15.37) * mm, v(-50.45, 13.61) * mm, v(-51.62, 11.52) * mm, v(-51.95, 10.52) * mm, v(-51.95, 9.89) * mm, v(-51.12, 9.85) * mm, v(-49.6, 10.4) * mm, v(-48.27, 11.19) * mm, v(-46.76, 12.27) * mm, v(-45.43, 13.24) * mm, v(-44.38, 13.95) * mm], "startDerivative": vector(-13.02, -11.66) * mm, "endDerivative": vector(13.48, 9.05) * mm});
            skFitSpline(sketch, "E123", {"points": [v(-49.36, 8.34) * mm, v(-50.32, 7.67) * mm, v(-51.53, 6.42) * mm, v(-52.46, 5.08) * mm, v(-51.53, 3.74) * mm, v(-51.37, 2.73) * mm, v(-51.28, -3.96) * mm, v(-51.45, -4.63) * mm, v(-52.04, -5.47) * mm, v(-53.2, -6.22) * mm, v(-52.88, -6.96) * mm, v(-51.47, -8.5) * mm, v(-50.33, -9.43) * mm, v(-49.4, -10.02) * mm, v(-48.65, -9.53) * mm, v(-47.13, -8.04) * mm, v(-46.26, -6.5) * mm, v(-46.1, -5.95) * mm, v(-47.08, -5.03) * mm, v(-47.67, -4.38) * mm, v(-47.84, -3.24) * mm, v(-47.94, 3.03) * mm, v(-47.78, 3.92) * mm, v(-47.21, 4.84) * mm, v(-46.97, 5.17) * mm, v(-47.02, 5.55) * mm, v(-48.13, 6.93) * mm, v(-49.36, 8.34) * mm]});
            skFitSpline(sketch, "E124", {"points": [v(-33.03, 3.34) * mm, v(-32.77, 4.26) * mm, v(-32.17, 5.1) * mm, v(-32, 5.39) * mm, v(-32.07, 5.74) * mm, v(-33.17, 7.2) * mm, v(-34.04, 8.1) * mm, v(-34.3, 8.27) * mm, v(-34.65, 8.12) * mm, v(-35.37, 7.4) * mm, v(-36.57, 6.48) * mm, v(-37.62, 6.02) * mm, v(-38.75, 5.99) * mm, v(-40.12, 6.44) * mm, v(-41.35, 7.36) * mm, v(-41.86, 7.92) * mm, v(-42, 8.06) * mm, v(-42.15, 8.12) * mm, v(-42.4, 8) * mm, v(-43.13, 7.34) * mm, v(-43.9, 6.48) * mm, v(-44.6, 5.6) * mm, v(-44.9, 5.21) * mm, v(-44.96, 5.04) * mm, v(-44.82, 4.72) * mm, v(-44.52, 4.25) * mm, v(-44.33, 3.98) * mm, v(-44.12, 3.65) * mm], "startDerivative": vector(3.75, 21.25) * mm, "endDerivative": vector(7.67, -12.75) * mm});
            skFitSpline(sketch, "E125", {"points": [v(-40.75, 2.67) * mm, v(-40.28, 3.54) * mm, v(-39.14, 4.03) * mm, v(-37.8, 4.07) * mm, v(-36.76, 3.49) * mm, v(-36.33, 2.6) * mm], "startDerivative": vector(1.78, 5.2) * mm, "endDerivative": vector(1.63, -5.1) * mm});
            skFitSpline(sketch, "E126", {"points": [v(-32.9, -3.77) * mm, v(-32.57, -4.4) * mm, v(-32, -5.08) * mm, v(-31.39, -5.6) * mm, v(-31.16, -5.82) * mm, v(-31.27, -6.2) * mm, v(-31.88, -7.3) * mm, v(-33.27, -8.8) * mm, v(-34.08, -9.4) * mm, v(-34.47, -9.62) * mm, v(-34.78, -9.44) * mm, v(-35.63, -8.77) * mm, v(-36.93, -7.64) * mm, v(-37.81, -6.55) * mm, v(-37.95, -6.27) * mm, v(-37.72, -5.97) * mm, v(-36.93, -5.43) * mm, v(-36.33, -4.87) * mm, v(-36.33, -4.55) * mm, v(-36.33, -4.34) * mm], "startDerivative": vector(5.52, -12.4) * mm, "endDerivative": vector(0.48, 7.16) * mm});
            skFitSpline(sketch, "E127", {"points": [v(-40.75, -3.66) * mm, v(-40.59, -4.34) * mm, v(-39.9, -5.08) * mm, v(-39.1, -5.69) * mm, v(-38.84, -5.89) * mm, v(-38.93, -6.28) * mm, v(-39.52, -7.37) * mm, v(-41.46, -9.3) * mm, v(-42.08, -9.73) * mm, v(-42.34, -9.73) * mm, v(-42.84, -9.47) * mm, v(-45.13, -7.41) * mm, v(-45.61, -6.72) * mm, v(-45.64, -6.39) * mm, v(-45.27, -6.02) * mm, v(-44.5, -5.4) * mm, v(-44.12, -5.08) * mm, v(-44.12, -4.8) * mm], "startDerivative": vector(1.18, -12.53) * mm, "endDerivative": vector(-1.63, 8.17) * mm});
            skFitSpline(sketch, "E128", {"points": [v(-26.5, 7.68) * mm, v(-26.37, 7.09) * mm, v(-26.48, 6.65) * mm, v(-27.5, 6.19) * mm, v(-28.84, 5.6) * mm, v(-29.9, 5) * mm, v(-30.38, 4.34) * mm, v(-30.44, 3.34) * mm, v(-30.43, -5.08) * mm, v(-30.4, -5.49) * mm, v(-29.76, -6.52) * mm, v(-27.07, -8.3) * mm, v(-25.06, -9.14) * mm, v(-24.72, -9.24) * mm, v(-24.38, -9.18) * mm, v(-23.02, -7.9) * mm, v(-20.64, -5.23) * mm, v(-19.05, -2.95) * mm, v(-18.92, -2.3) * mm, v(-19.1, -1.2) * mm, v(-19.5, -0.04) * mm, v(-20.36, 1.92) * mm], "startDerivative": vector(5.75, -19.57) * mm, "endDerivative": vector(-15.94, 36.18) * mm});
            skFitSpline(sketch, "E129", {"points": [v(-27.18, 3.19) * mm, v(-26.96, 3.92) * mm, v(-26.3, 4.44) * mm, v(-25.44, 4.46) * mm, v(-25, 3.9) * mm], "startDerivative": vector(0.53, 3.15) * mm, "endDerivative": vector(1.42, -2.93) * mm});
            skFitSpline(sketch, "E130", {"points": [v(-22.62, -1.86) * mm, v(-22.43, -2.56) * mm, v(-22.43, -3.43) * mm, v(-23.62, -5.17) * mm, v(-24, -5.39) * mm, v(-24.6, -5.39) * mm, v(-25.58, -4.98) * mm, v(-26.44, -4.36) * mm, v(-27.1, -3.27) * mm, v(-27.18, -2.48) * mm], "startDerivative": vector(1.99, -7.25) * mm, "endDerivative": vector(0.09, 7.38) * mm});
            skFitSpline(sketch, "E131", {"points": [v(-12.08, -4.65) * mm, v(-12.67, -2.48) * mm, v(-12.58, -0.04) * mm, v(-11.91, 3.05) * mm, v(-11.86, 3.14) * mm, v(-12.2, 3.02) * mm, v(-13.75, 1.95) * mm, v(-15.06, -0.04) * mm, v(-15.73, -2.07) * mm, v(-15.95, -4.23) * mm, v(-16, -6.42) * mm, v(-16.01, -6.71) * mm, v(-16.01, -6.8) * mm, v(-13.95, -5.58) * mm, v(-12.27, -4.7) * mm], "startDerivative": vector(-8.11, 24.7) * mm, "endDerivative": vector(17.5, 8) * mm});
            skFitSpline(sketch, "E132", {"points": [v(-4.43, -6.18) * mm, v(-4, -5.78) * mm, v(-3.84, -5.2) * mm], "startDerivative": vector(1, 0.73) * mm, "endDerivative": vector(0.2, 1.22) * mm});
            skFitSpline(sketch, "E133", {"points": [v(-3.84, 12.28) * mm, v(-2.14, 13.6) * mm, v(-1.54, 13.8) * mm, v(-0.94, 13.78) * mm, v(-0.17, 13.29) * mm, v(0.9, 12.48) * mm, v(2.68, 11.54) * mm, v(4.55, 11.25) * mm, v(6.3, 11.46) * mm, v(7.47, 12.28) * mm, v(7.62, 12.5) * mm, v(7.64, 12.55) * mm, v(6.1, 13.15) * mm, v(4.2, 14.6) * mm, v(2.78, 16.44) * mm, v(1.55, 18.96) * mm, v(1.35, 19.49) * mm], "startDerivative": vector(23.38, 19.98) * mm, "endDerivative": vector(-3.54, 9.98) * mm});
            skFitSpline(sketch, "E134", {"points": [v(52.4, 7.87) * mm, v(52.54, 7.28) * mm, v(52.43, 6.85) * mm, v(51.4, 6.38) * mm, v(50.07, 5.79) * mm, v(49, 5.2) * mm, v(48.52, 4.54) * mm, v(48.47, 3.54) * mm, v(48.47, -4.88) * mm, v(48.5, -5.3) * mm, v(49.14, -6.32) * mm, v(51.83, -8.1) * mm, v(53.85, -8.95) * mm, v(54.19, -9.04) * mm, v(54.53, -8.99) * mm, v(55.89, -7.71) * mm, v(58.27, -5.04) * mm, v(59.85, -2.76) * mm, v(59.98, -2.1) * mm, v(59.81, -1.01) * mm, v(59.4, 0.16) * mm, v(58.55, 2.12) * mm], "startDerivative": vector(5.75, -19.57) * mm, "endDerivative": vector(-15.94, 36.18) * mm});
            skFitSpline(sketch, "E135", {"points": [v(51.73, 3.38) * mm, v(51.95, 4.11) * mm, v(52.6, 4.63) * mm, v(53.46, 4.66) * mm, v(53.9, 4.09) * mm], "startDerivative": vector(0.53, 3.15) * mm, "endDerivative": vector(1.42, -2.93) * mm});
            skFitSpline(sketch, "E136", {"points": [v(56.29, -1.67) * mm, v(56.48, -2.37) * mm, v(56.48, -3.24) * mm, v(55.28, -4.98) * mm, v(54.9, -5.2) * mm, v(54.3, -5.2) * mm, v(53.33, -4.79) * mm, v(52.46, -4.16) * mm, v(51.8, -3.08) * mm, v(51.73, -2.29) * mm], "startDerivative": vector(1.99, -7.25) * mm, "endDerivative": vector(0.09, 7.38) * mm});
            skFitSpline(sketch, "E137", {"points": [v(65.7, 18.33) * mm, v(64.53, 17.24) * mm, v(62.86, 15.4) * mm, v(61.69, 13.65) * mm, v(60.52, 11.55) * mm, v(60.18, 10.55) * mm, v(60.18, 9.92) * mm, v(61.02, 9.88) * mm, v(62.53, 10.42) * mm, v(63.86, 11.22) * mm, v(65.37, 12.3) * mm, v(66.7, 13.27) * mm, v(67.76, 13.98) * mm], "startDerivative": vector(-13.02, -11.66) * mm, "endDerivative": vector(13.48, 9.05) * mm});
            skFitSpline(sketch, "E138", {"points": [v(62.78, 8.37) * mm, v(61.81, 7.7) * mm, v(60.6, 6.45) * mm, v(59.68, 5.1) * mm, v(60.6, 3.77) * mm, v(60.77, 2.77) * mm, v(60.85, -3.93) * mm, v(60.68, -4.6) * mm, v(60.1, -5.43) * mm, v(58.93, -6.19) * mm, v(59.25, -6.92) * mm, v(60.66, -8.47) * mm, v(61.8, -9.4) * mm, v(62.73, -9.99) * mm, v(63.49, -9.5) * mm, v(65, -8) * mm, v(65.87, -6.46) * mm, v(66.04, -5.92) * mm, v(65.06, -5) * mm, v(64.46, -4.35) * mm, v(64.3, -3.2) * mm, v(64.2, 3.06) * mm, v(64.35, 3.96) * mm, v(64.92, 4.88) * mm, v(65.17, 5.2) * mm, v(65.11, 5.58) * mm, v(64, 6.97) * mm, v(62.78, 8.37) * mm]});
            skFitSpline(sketch, "E139", {"points": [v(7.42, -10.2) * mm, v(7.63, -12.34) * mm, v(9.05, -15.25) * mm, v(10.63, -17.04) * mm, v(10.72, -17.11) * mm, v(10.6, -17.11) * mm, v(9.17, -17.04) * mm, v(6.72, -16.08) * mm, v(5.06, -14.44) * mm], "startDerivative": vector(0.17, -13.92) * mm, "endDerivative": vector(-9.57, 11.37) * mm});
            skFitSpline(sketch, "E140", {"points": [v(-14.13, -13.4) * mm, v(-12.99, -15.09) * mm, v(-10.5, -16.89) * mm, v(-7.4, -18.12) * mm, v(-4, -18.42) * mm, v(-0.9, -17.92) * mm, v(2.07, -16.64) * mm, v(4.47, -14.82) * mm, v(5.06, -14.44) * mm], "startDerivative": vector(8.5, -15.86) * mm, "endDerivative": vector(7.8, 4.28) * mm});
            skFitSpline(sketch, "E141", {"points": [v(-10.36, -11.11) * mm, v(-8.28, -13.14) * mm, v(-5.18, -14.72) * mm, v(-1.61, -14.68) * mm, v(1.51, -12.97) * mm, v(2.94, -10.45) * mm], "startDerivative": vector(10.06, -11.04) * mm, "endDerivative": vector(6.18, 13.54) * mm});
            skFitSpline(sketch, "E142", {"points": [v(10.19, -4.82) * mm, v(10.25, 1.64) * mm, v(10.25, 2.47) * mm, v(10.16, 2.86) * mm, v(9.72, 3.7) * mm, v(9.29, 4.17) * mm, v(9.11, 4.46) * mm, v(9.37, 4.83) * mm, v(10.8, 6.72) * mm, v(11.81, 7.6) * mm, v(12.15, 7.76) * mm, v(12.55, 7.5) * mm, v(14.24, 5.47) * mm, v(14.57, 4.96) * mm, v(14.1, 4.12) * mm, v(13.7, 3.14) * mm, v(13.56, -0.76) * mm, v(13.63, -4) * mm, v(13.67, -4.54) * mm, v(14.07, -5.21) * mm, v(15.28, -5.99) * mm, v(16.4, -6.02) * mm, v(17.47, -5.48) * mm, v(17.94, -4.74) * mm, v(17.98, -3.16) * mm, v(17.94, 2.13) * mm, v(17.94, 2.8) * mm, v(17.6, 3.62) * mm, v(16.87, 4.5) * mm, v(16.78, 4.76) * mm, v(17.25, 5.48) * mm, v(18.18, 6.59) * mm, v(19.32, 7.65) * mm, v(19.6, 7.82) * mm, v(19.9, 7.78) * mm, v(20.79, 6.86) * mm, v(21.58, 5.85) * mm, v(21.98, 5.28) * mm, v(22.1, 5.09) * mm, v(22, 4.83) * mm, v(21.43, 4.04) * mm, v(21.3, 3.84) * mm, v(21.24, 3.46) * mm, v(21.28, -3.67) * mm, v(21.28, -3.92) * mm, v(21.63, -4.78) * mm, v(22.58, -5.52) * mm, v(23.15, -5.63) * mm, v(23.26, -5.63) * mm, v(23.28, -5.82) * mm, v(22.97, -6.84) * mm, v(21.6, -8.54) * mm, v(20.08, -9.75) * mm, v(19.84, -9.83) * mm, v(19.5, -9.66) * mm, v(18.45, -8.95) * mm, v(16.83, -8.25) * mm, v(15.87, -8.08) * mm, v(14.57, -8.27) * mm, v(12.33, -9.73) * mm, v(11.97, -10.13) * mm, v(11.77, -10.2) * mm, v(11.12, -9.78) * mm, v(9.8, -8.64) * mm, v(8.74, -7.43) * mm, v(8.52, -7.13) * mm, v(8.57, -6.77) * mm, v(9.42, -6.22) * mm, v(10.12, -5.53) * mm, v(10.19, -4.82) * mm]});
            skFitSpline(sketch, "E143", {"points": [v(36.88, -6.22) * mm, v(38.1, -5.21) * mm, v(38.45, -4.03) * mm, v(38.4, 2.82) * mm, v(38.38, 3.27) * mm, v(38.27, 3.67) * mm, v(37.56, 4.55) * mm, v(37.39, 4.75) * mm, v(37.4, 5.05) * mm, v(39.2, 7.26) * mm, v(39.98, 7.94) * mm, v(40.22, 8.05) * mm, v(40.57, 7.9) * mm, v(41.8, 6.65) * mm, v(42.32, 6.06) * mm, v(42.5, 5.97) * mm, v(42.67, 6.1) * mm, v(44.02, 7.28) * mm, v(44.96, 7.96) * mm, v(45.29, 8.07) * mm, v(45.64, 7.8) * mm, v(46.51, 6.85) * mm, v(47.3, 5.75) * mm, v(47.56, 4.46) * mm, v(47.21, 2.72) * mm, v(46.51, 1.08) * mm, v(45.55, -0.32) * mm, v(44.41, -1.41) * mm, v(44.27, -1.54) * mm, v(44.27, -1.41) * mm, v(44.32, 0.79) * mm, v(44.23, 2.3) * mm, v(43.38, 4.04) * mm, v(42.81, 4.72) * mm, v(42.55, 4.8) * mm, v(42.16, 4.55) * mm, v(41.8, 3.98) * mm, v(41.72, 2.71) * mm, v(41.73, -3.84) * mm, v(41.77, -4.09) * mm, v(42.2, -4.8) * mm, v(42.99, -5.39) * mm, v(44, -5.43) * mm, v(44.94, -5.43) * mm, v(45.11, -5.45) * mm, v(45.09, -5.57) * mm, v(44.65, -6.52) * mm, v(43.71, -7.57) * mm, v(42.48, -8.48) * mm, v(41.06, -9.3) * mm, v(40.23, -9.65) * mm, v(40.07, -9.67) * mm, v(39.76, -9.56) * mm, v(38.68, -8.77) * mm, v(37.98, -8.1) * mm, v(37.13, -7.2) * mm, v(36.67, -6.67) * mm, v(36.64, -6.52) * mm, v(36.7, -6.35) * mm, v(36.88, -6.22) * mm]});
            skFitSpline(sketch, "E144", {"points": [v(9.29, -13.57) * mm, v(8.85, -12.68) * mm, v(8.6, -11.78) * mm, v(8.6, -11.08) * mm], "startDerivative": vector(-1.32, 2.47) * mm, "endDerivative": vector(0.14, 2.27) * mm});
            skFitSpline(sketch, "E145", {"points": [v(36.17, -6.62) * mm, v(35.43, -7.8) * mm, v(34.32, -8.79) * mm, v(33.67, -9.2) * mm, v(33.26, -9.06) * mm, v(32.37, -8.51) * mm, v(31.28, -7.92) * mm, v(30.52, -7.78) * mm, v(29.57, -7.97) * mm, v(28.68, -8.57) * mm, v(28.13, -8.98) * mm, v(27.86, -9.22) * mm, v(27.27, -8.87) * mm, v(25.96, -7.8) * mm, v(24.66, -5.96) * mm, v(23.69, -4.12) * mm, v(22.65, -1.68) * mm, v(22.38, -0.32) * mm, v(23.17, 1.69) * mm, v(24.34, 3.78) * mm, v(26, 5.81) * mm, v(27.94, 7.11) * mm, v(29.7, 7.33) * mm, v(31.6, 6.7) * mm, v(33.29, 6.06) * mm, v(34.65, 6.03) * mm, v(35.65, 6.06) * mm, v(35.8, 6.07) * mm, v(35.75, 5.92) * mm, v(35.18, 5.26) * mm, v(34.8, 4.71) * mm, v(34.67, 3.9) * mm, v(34.67, 0.82) * mm], "startDerivative": vector(-19.03, -37.74) * mm, "endDerivative": vector(0.67, -72.98) * mm});
            skFitSpline(sketch, "E146", {"points": [v(34.67, 0.82) * mm, v(34.67, -3.03) * mm, v(34.67, -3.66) * mm, v(34.67, -4.07) * mm, v(35.32, -5.2) * mm, v(35.94, -5.91) * mm, v(36.21, -6.26) * mm, v(36.17, -6.62) * mm], "startDerivative": vector(-0.08, -16.07) * mm, "endDerivative": vector(-1.27, -4.14) * mm});
            skFitSpline(sketch, "E147", {"points": [v(31, -4.46) * mm, v(30.74, -5.13) * mm, v(29.95, -5.46) * mm, v(28.95, -5.13) * mm, v(28.07, -3.62) * mm, v(27.15, -1.7) * mm, v(26.27, 0.4) * mm, v(26.23, 1.4) * mm, v(27.06, 2.9) * mm, v(28.23, 3.74) * mm, v(29.4, 3.74) * mm, v(30.41, 2.99) * mm, v(31.08, 1.82) * mm, v(31.08, 1.27) * mm, v(31, -4.46) * mm]});
            skFitSpline(sketch, "E148", {"points": [v(78.86, -6.38) * mm, v(78.13, -7.57) * mm, v(77.02, -8.55) * mm, v(76.36, -8.96) * mm, v(75.96, -8.82) * mm, v(75.06, -8.28) * mm, v(73.98, -7.68) * mm, v(73.22, -7.55) * mm, v(72.27, -7.74) * mm, v(71.37, -8.33) * mm, v(70.83, -8.74) * mm, v(70.56, -8.99) * mm, v(69.96, -8.63) * mm, v(68.66, -7.57) * mm, v(67.36, -5.73) * mm, v(66.38, -3.89) * mm, v(65.35, -1.44) * mm, v(65.08, -0.09) * mm, v(65.86, 1.92) * mm, v(67.03, 4.01) * mm, v(68.69, 6.04) * mm, v(70.64, 7.35) * mm, v(72.4, 7.56) * mm, v(74.3, 6.94) * mm, v(75.98, 6.29) * mm, v(77.34, 6.26) * mm, v(78.34, 6.3) * mm, v(78.5, 6.3) * mm, v(78.44, 6.15) * mm, v(77.88, 5.5) * mm, v(77.5, 4.95) * mm, v(77.37, 4.14) * mm, v(77.36, 1.05) * mm], "startDerivative": vector(-19.03, -37.74) * mm, "endDerivative": vector(0.67, -72.98) * mm});
            skFitSpline(sketch, "E149", {"points": [v(77.36, 1.05) * mm, v(77.36, -2.8) * mm, v(77.36, -3.42) * mm, v(77.36, -3.83) * mm, v(78.01, -4.97) * mm, v(78.64, -5.68) * mm, v(78.9, -6.03) * mm, v(78.86, -6.38) * mm], "startDerivative": vector(-0.08, -16.07) * mm, "endDerivative": vector(-1.27, -4.14) * mm});
            skFitSpline(sketch, "E150", {"points": [v(73.7, -4.22) * mm, v(73.44, -4.9) * mm, v(72.64, -5.23) * mm, v(71.64, -4.9) * mm, v(70.76, -3.39) * mm, v(69.84, -1.46) * mm, v(68.96, 0.63) * mm, v(68.92, 1.63) * mm, v(69.76, 3.14) * mm, v(70.93, 3.98) * mm, v(72.1, 3.98) * mm, v(73.1, 3.22) * mm, v(73.77, 2.05) * mm, v(73.77, 1.5) * mm, v(73.7, -4.22) * mm]});
            skFitSpline(sketch, "E151", {"points": [v(84.7, -17.25) * mm, v(85.85, -16.04) * mm, v(87.6, -14.05) * mm, v(88.95, -11.59) * mm, v(89.66, -9.64) * mm, v(89.7, -9.31) * mm, v(89, -9.6) * mm, v(86.8, -10.97) * mm, v(84.35, -12.73) * mm, v(82.89, -13.85) * mm, v(82.73, -14) * mm, v(83.55, -15.04) * mm, v(84.42, -16.28) * mm, v(84.61, -16.85) * mm, v(84.68, -17.16) * mm], "startDerivative": vector(13.55, 14.48) * mm, "endDerivative": vector(1.8, -8.49) * mm});
            skFitSpline(sketch, "E152", {"points": [v(94.31, 10.77) * mm, v(93.78, 11.46) * mm, v(92.9, 12.07) * mm, v(91.92, 12.18) * mm], "startDerivative": vector(-1.51, 2.2) * mm, "endDerivative": vector(-2.98, -0.02) * mm});
            skFitSpline(sketch, "E153", {"points": [v(94.9, 17.88) * mm, v(95.86, 16.94) * mm, v(97.67, 15.48) * mm, v(100.03, 14.04) * mm, v(100.92, 13.64) * mm, v(101.03, 13.6) * mm, v(100.97, 13.53) * mm, v(100.3, 12.85) * mm, v(99.65, 12.18) * mm, v(99.6, 12.09) * mm, v(99.59, 11.92) * mm, v(99.45, -7.01) * mm, v(99.45, -7.52) * mm, v(99.45, -7.93) * mm, v(99.87, -8.9) * mm, v(101.12, -10.45) * mm, v(101.63, -10.86) * mm, v(101.54, -11.23) * mm, v(99.49, -14.18) * mm, v(98.17, -15.58) * mm, v(97.83, -15.82) * mm, v(97.35, -15.68) * mm, v(94.9, -13.92) * mm, v(93.58, -12.45) * mm, v(93.36, -11.43) * mm, v(93.58, -10.47) * mm, v(94.31, -9.59) * mm, v(94.47, -8.66) * mm], "startDerivative": vector(22.84, -23.48) * mm, "endDerivative": vector(0.1, 30.15) * mm});
            skSolve(sketch);
        }
        {
            var Q0;
            Q0 = qSketchRegion(id + "F0", true);
            extrude(context, id + "F1", {"entities" : qUnion([Q0]), "depth" : 6 * mm, "offsetDistance" : 25 * mm});
        }
        {
            var Q0;
            Q0=qCreatedBy(makeId("Right.planeOp"),FACE);
            var sketch = newSketch(context, id + "F2", { "sketchPlane" : qUnion([Q0])});
            skLineSegment(sketch, "E154", {"start": v(-70, 25) * mm, "end": v(110, 25) * mm});
            skLineSegment(sketch, "E155", {"start": v(-70, 25) * mm, "end": v(-95, 7.5) * mm});
            skLineSegment(sketch, "E156", {"start": v(-95, 7.5) * mm, "end": v(-95, -25) * mm});
            skLineSegment(sketch, "E157", {"start": v(-95, -25) * mm, "end": v(110, -25) * mm});
            skLineSegment(sketch, "E158", {"start": v(110, -25) * mm, "end": v(110, 25) * mm});
            skSolve(sketch);
        }
        {
            var Q0;
            Q0 = qSketchRegion(id + "F2", true);
            extrude(context, id + "F3", {"entities" : qUnion([Q0]), "operationType" : NewBodyOperationType.ADD, "oppositeDirection" : true, "depth" : 4 * mm, "offsetDistance" : 25 * mm});
        }
    });
